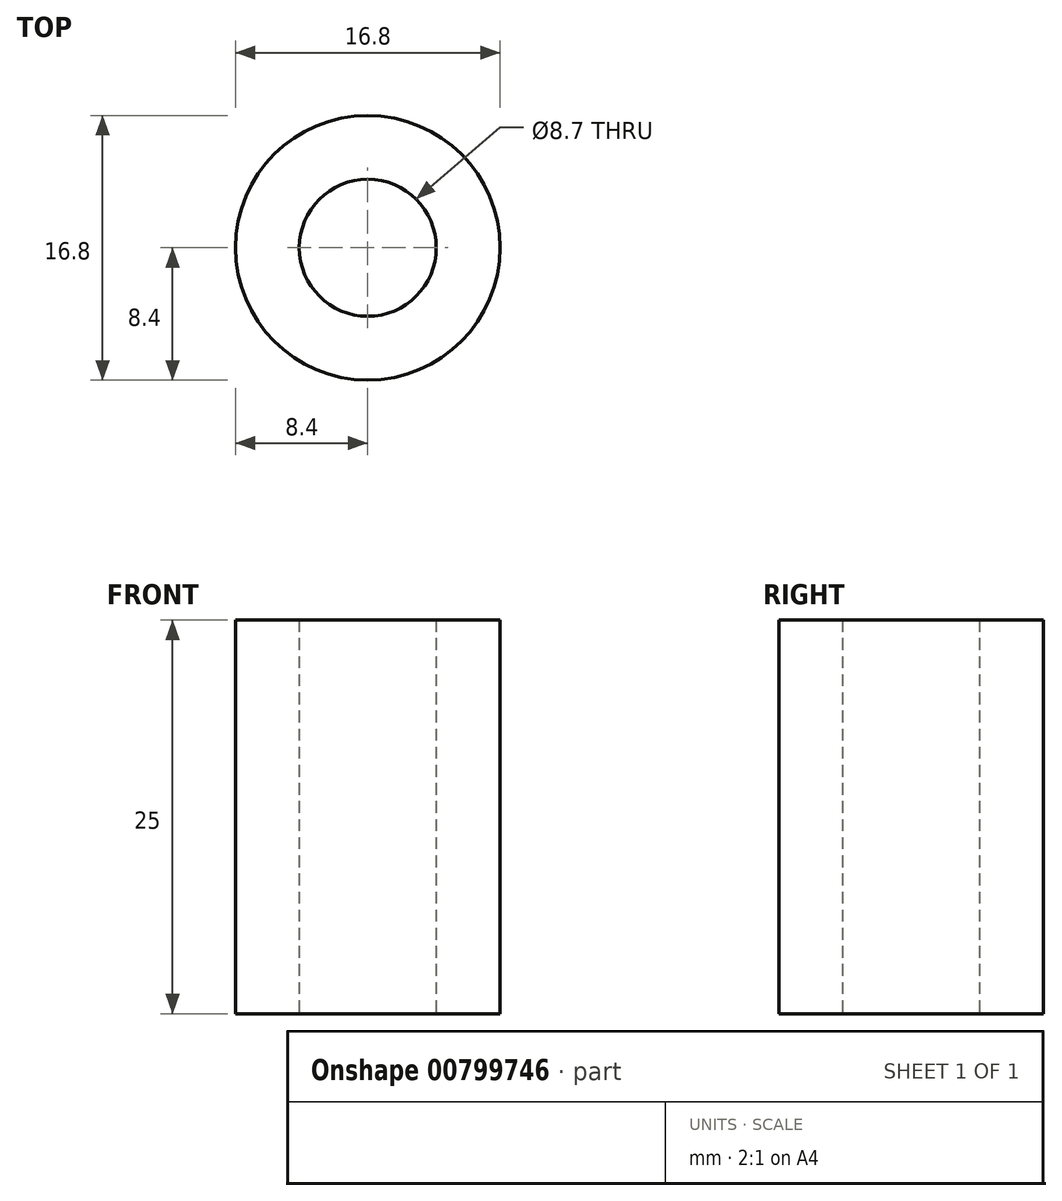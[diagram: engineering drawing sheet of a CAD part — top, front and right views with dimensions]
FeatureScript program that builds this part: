
annotation { "Feature Type Name" : "Feature", "Feature Type Description" : "" }
export const myFeature = defineFeature(function(context is Context, id is Id, definition is map)
    precondition{}
    {
        {
            var Q0;
            Q0=qCreatedBy(makeId("Top.planeOp"),FACE);
            var sketch = newSketch(context, id + "F0", { "sketchPlane" : qUnion([Q0])});
            skCircle(sketch, "E0", {"center": v(0, 0) * mm, "radius": 4.35 * mm});
            skCircle(sketch, "E1", {"center": v(0, 0) * mm, "radius": 8.4 * mm});
            skSolve(sketch);
        }
        {
            var Q0;
            Q0=makeQuery(id+"F0.imprint","IMPRINT",FACE,{"disambiguationData":[TD([[makeQuery(id+"F0.imprint","IMPRINT",EDGE,{"derivedFrom":sQuery(id+"F0.wireOp",EDGE,"E0")}),-1.0]])]});
            extrude(context, id + "F1", {"entities" : qUnion([Q0]), "depth" : 25 * mm, "offsetDistance" : 25 * mm});
        }
    });
